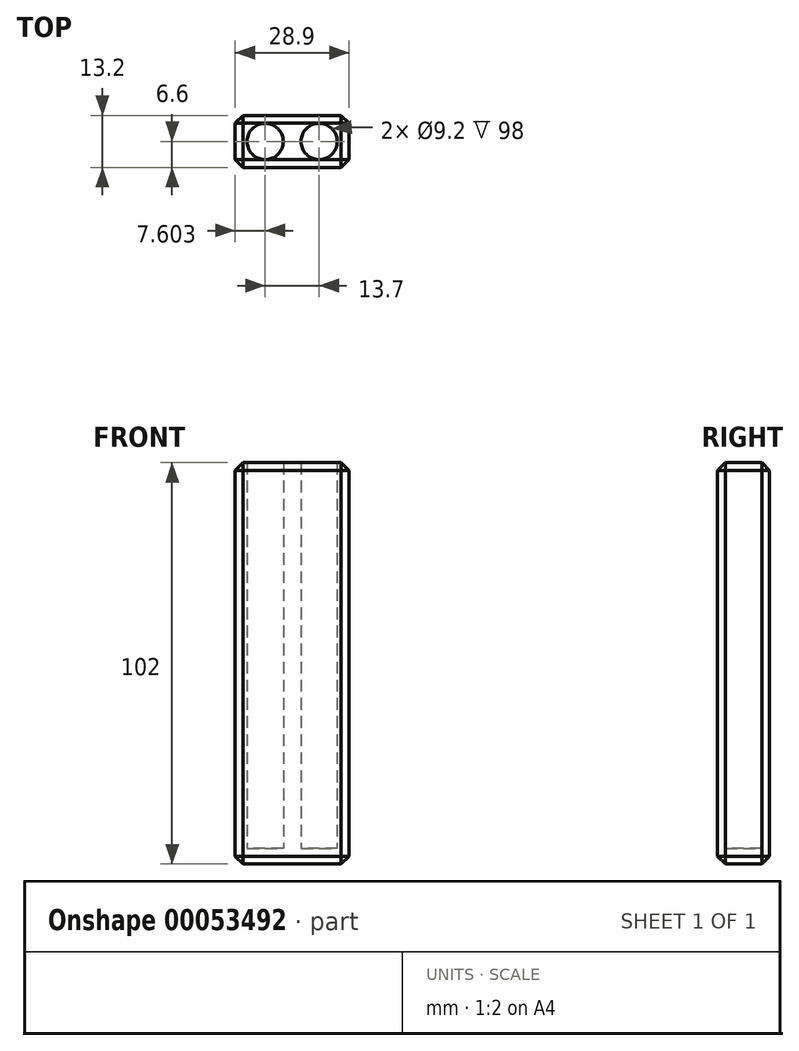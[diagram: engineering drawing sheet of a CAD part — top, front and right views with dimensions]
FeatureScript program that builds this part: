
annotation { "Feature Type Name" : "Feature", "Feature Type Description" : "" }
export const myFeature = defineFeature(function(context is Context, id is Id, definition is map)
    precondition{}
    {
        {
            var Q0;
            Q0=qCreatedBy(makeId("Top.planeOp"),FACE);
            var sketch = newSketch(context, id + "F0", { "sketchPlane" : qUnion([Q0])});
            skCircle(sketch, "E0", {"center": v(-18.18, 0) * mm, "radius": 4.6 * mm});
            skCircle(sketch, "E1", {"center": v(-4.48, 0) * mm, "radius": 4.6 * mm});
            skLineSegment(sketch, "E2.bottom", {"start": v(-25.78, 6.6) * mm, "end": v(3.12, 6.6) * mm});
            skLineSegment(sketch, "E2.top", {"start": v(-25.78, -6.6) * mm, "end": v(3.12, -6.6) * mm});
            skLineSegment(sketch, "E2.left", {"start": v(-25.78, 6.6) * mm, "end": v(-25.78, -6.6) * mm});
            skLineSegment(sketch, "E2.right", {"start": v(3.12, 6.6) * mm, "end": v(3.12, -6.6) * mm});
            skSolve(sketch);
        }
        {
            var Q0;
            Q0=makeQuery(id+"F0.imprint","IMPRINT",FACE,{"disambiguationData":[TD([[makeQuery(id+"F0.imprint","IMPRINT",EDGE,{"derivedFrom":sQuery(id+"F0.wireOp",EDGE,"E0")}),-1.0]])]});
            extrude(context, id + "F1", {"entities" : qUnion([Q0]), "depth" : 98 * mm});
        }
        {
            var Q0;
            Q0=makeQuery(id+"F0.imprint","IMPRINT",FACE,{"disambiguationData":[TD([[makeQuery(id+"F0.imprint","IMPRINT",EDGE,{"derivedFrom":sQuery(id+"F0.wireOp",EDGE,"E1")}),1.0]])]});
            var Q1;
            Q1=makeQuery(id+"F0.imprint","IMPRINT",FACE,{"disambiguationData":[TD([[makeQuery(id+"F0.imprint","IMPRINT",EDGE,{"derivedFrom":sQuery(id+"F0.wireOp",EDGE,"E0")}),-1.0]])]});
            var Q2;
            Q2=makeQuery(id+"F0.imprint","IMPRINT",FACE,{"disambiguationData":[TD([[makeQuery(id+"F0.imprint","IMPRINT",EDGE,{"derivedFrom":sQuery(id+"F0.wireOp",EDGE,"E0")}),1.0]])]});
            extrude(context, id + "F2", {"entities" : qUnion([Q0, Q1, Q2]), "operationType" : NewBodyOperationType.ADD, "oppositeDirection" : true, "depth" : 4 * mm});
        }
        {
            var Q0;
            {var subQ0=sQuery(id+"F0.wireOp",EDGE,"E2.top");Q0=makeQuery(id+"F2.boolean.opBoolean","MERGE",FACE,{"derivedFrom":[makeQuery(id+"F1.opExtrude","SWEPT_FACE",FACE,{"disambiguationData":[OSD([subQ0])]}),makeQuery(id+"F2.opExtrude","SWEPT_FACE",FACE,{"disambiguationData":[OSD([subQ0])]})]});}
            var Q1;
            {var subQ0=sQuery(id+"F0.wireOp",EDGE,"E2.left");Q1=makeQuery(id+"F2.boolean.opBoolean","MERGE",FACE,{"derivedFrom":[makeQuery(id+"F1.opExtrude","SWEPT_FACE",FACE,{"disambiguationData":[OSD([subQ0])]}),makeQuery(id+"F2.opExtrude","SWEPT_FACE",FACE,{"disambiguationData":[OSD([subQ0])]})]});}
            var Q2;
            {var subQ0=sQuery(id+"F0.wireOp",EDGE,"E2.bottom");Q2=makeQuery(id+"F2.boolean.opBoolean","MERGE",FACE,{"derivedFrom":[makeQuery(id+"F1.opExtrude","SWEPT_FACE",FACE,{"disambiguationData":[OSD([subQ0])]}),makeQuery(id+"F2.opExtrude","SWEPT_FACE",FACE,{"disambiguationData":[OSD([subQ0])]})]});}
            var Q3;
            {var subQ0=sQuery(id+"F0.wireOp",EDGE,"E2.right");Q3=makeQuery(id+"F2.boolean.opBoolean","MERGE",FACE,{"derivedFrom":[makeQuery(id+"F1.opExtrude","SWEPT_FACE",FACE,{"disambiguationData":[OSD([subQ0])]}),makeQuery(id+"F2.opExtrude","SWEPT_FACE",FACE,{"disambiguationData":[OSD([subQ0])]})]});}
            chamfer(context, id + "F3", {"entities" : qUnion([Q0, Q1, Q2, Q3]), "width" : 2 * mm, "tangentPropagation" : true});
        }
    });
